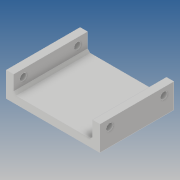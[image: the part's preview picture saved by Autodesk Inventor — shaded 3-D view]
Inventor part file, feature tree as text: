
AUTODESK INVENTOR PART (.ipt)
format: ipt  version: 2019 (Build 230136000, 136)  size: 115,200 bytes
history: native  units: mm
features: sketch x3, extrude x2, chamfer x1, hole x1
ambient origin geometry x8: Origin, YZ Plane, XZ Plane, XY Plane, X Axis, Y Axis, Z Axis, Center Point
bodies: Solide1 (feature_tree)
feature tree (7):
  extrude  "Extrusion1"  Depth=76.0mm
  extrude  "Extrusion2"  Depth=60.0mm
  chamfer  "Chanfrein1"  Distance=6.0mm
  hole  "Perçage1"  [1 undecoded]
  sketch  "Esquisse1"
  sketch  "Esquisse2"
  sketch  "Esquisse4"
note: 1 required parameter value undecoded (feature->parameter linkage not recoverable at this tier; creation-order binding heuristic only, values carry confidence <= 0.55)
